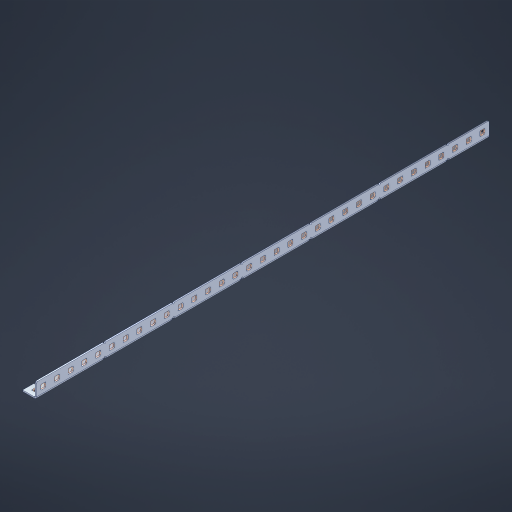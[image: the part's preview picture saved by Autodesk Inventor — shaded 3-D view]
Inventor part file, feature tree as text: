
AUTODESK INVENTOR PART (.ipt)
format: ipt  version: 2023 (Build 270158000, 158)  size: 1,292,800 bytes
history: native  units: in
note: dims shown in document units (in); Inventor stores cm internally (conversion verified against a paired STEP export)
features: other x106, extrude x97, sheet_metal_op x11, sketch x10, pattern_linear x2, mirror x1, chamfer x1
ambient origin geometry x8: Origin, YZ Plane, XZ Plane, XY Plane, X Axis, Y Axis, Z Axis, Center Point
bodies: Solid1 (feature_tree), Body (feature_tree)
feature tree (228):
  sheet_metal_op  "Flanges"
  other  "Flange Pattern Plane"
  other  "Flange Pattern Sketch"
  sheet_metal_op  "Flange Pattern"
  sheet_metal_op  "Body Pattern"
  pattern_linear  "Center Pattern"  Spacing1=0.0469in  [1 undecoded]
  other  "Arc Length"
  mirror  "Notch Mirror"
  pattern_linear  "Notch Pattern"  Spacing1=0.182in  [1 undecoded]
  chamfer  "End Chamfer"
  extrude  "Half Cut"  Depth=0.02in
  sketch  "Sketch1"  dims[d0=1.0in]
  other  "Plate1"
  sketch  "Sketch2"  dims[d1=16.5in]
  other  "Plate2"
  sheet_metal_op  "Bend1"
  sheet_metal_op  "Corner1"
  sketch  "Sketch3"  dims[d2=0.0469in]
  sketch  "Sketch7"  dims[d3=0.0469in]
  other  "Srf1"
  other  "Srf2"
  sketch  "Sketch8"  dims[d4=0.0234in]
  sketch  "Sketch9"  dims[d5=0.0938in]
  other  "Srf91"
  sheet_metal_op  "Body Pattern Sketch"
  other  "Srf92"
  sketch  "Sketch13"  dims[d6=0.0469in]
  sketch  "Sketch14"  dims[d7=0.5in d8=90.0deg d9=0.0312in]
  sketch  "Sketch15"  dims[d10=0.1875in]
  sketch  "Sketch16"  dims[d11=0.0469in d12=0.0469in d16=0.182in d17=0.02in d18=0.0469in d19=0.0in d20=0.25in d21=0.25in d38=12.9921in d40=0.5in d41=0.3937in d43=1.0in d46=0.172in d47=1.0in d48=0.0in d49=0.182in d50=0.02in d51=0.25in d52=0.25in d53=0.0469in d54=0.0in d55=0.172in d56=1.0in d57=0.0in d58=0.25in d60=12.9921in d62=0.5in d63=0.3937in d65=0.5in d85=0.1227in d86=0.1659in d88=0.04in d89=0.0469in d90=0.0in d91=0.04in d92=0.0491in d95=2.5in d96=0.04in d97=0.25in d98=45.0deg d99=0.25in d100=0.5in d101=0.0in d102=2.497in d106=0.182in d107=0.02in d108=0.5in d109=0.5in d110=0.0469in d111=0.0in d112=0.172in d113=0.5in d114=0.0in d117=0.5in d118=0.5in d119=0.5in]
  other  "Srf786"
  other  "Srf823"
  other  "Srf824"
  other  "Srf825"
  other  "Srf826"
  other  "Srf827"
  other  "Srf828"
  other  "Srf829"
  other  "Srf856"
  other  "Srf857"
  other  "Srf858"
  other  "Srf859"
  other  "Srf860"
  other  "Srf861"
  other  "Srf862"
  other  "Srf889"
  other  "Srf890"
  other  "Srf891"
  other  "Srf892"
  other  "Srf893"
  other  "Srf894"
  other  "Srf895"
  other  "Srf896"
  other  "Srf922"
  other  "Srf923"
  other  "Srf924"
  other  "Srf925"
  other  "Srf926"
  other  "Srf959"
  other  "Srf960"
  other  "Srf961"
  other  "Srf962"
  other  "Srf963"
  other  "Srf996"
  other  "Srf997"
  other  "Srf998"
  other  "Srf999"
  other  "Srf1000"
  other  "Srf1143"
  other  "Srf1144"
  other  "Srf1145"
  other  "Srf1146"
  other  "Srf1147"
  other  "Srf1148"
  other  "Srf1149"
  other  "Srf1150"
  other  "Srf1151"
  other  "Srf1152"
  other  "Srf1153"
  other  "Srf1154"
  other  "Srf1155"
  other  "Srf1156"
  other  "Srf1157"
  other  "Srf1158"
  other  "Srf1159"
  other  "Srf1160"
  other  "Srf1161"
  other  "Srf1199"
  other  "Srf1200"
  other  "Srf1201"
  other  "Srf1202"
  other  "Srf1203"
  other  "Srf1204"
  other  "Srf1205"
  other  "Srf1206"
  other  "Srf1207"
  other  "Srf1208"
  other  "Srf1209"
  other  "Srf1210"
  other  "Srf1211"
  other  "Srf1212"
  other  "Srf1213"
  other  "Srf1214"
  other  "Srf1215"
  other  "Srf1216"
  other  "Srf1217"
  other  "Srf1255"
  other  "Srf1256"
  other  "Srf1257"
  other  "Srf1258"
  other  "Srf1259"
  other  "Srf1260"
  other  "Srf1261"
  other  "Srf1262"
  other  "Srf1263"
  other  "Srf1264"
  other  "Srf1265"
  other  "Srf1266"
  other  "Srf1267"
  other  "Srf1268"
  other  "Srf1269"
  other  "Srf1270"
  other  "Srf1271"
  other  "Srf1272"
  other  "Srf1273"
  sheet_metal_op  "Flange Stamp"
  sheet_metal_op  "Flange Circle"
  sheet_metal_op  "Body Stamp"
  sheet_metal_op  "Body Circle"
  other  "Center Stamp"
  other  "Center Circle"
  sheet_metal_op  "Notch"
  extrude  "ExtrusionSrf2"  Depth=0.0469in
  extrude  "ExtrusionSrf92"  TaperAngle=0.0deg  [1 undecoded]
  extrude  "ExtrusionSrf823"  Depth=0.5in
  extrude  "ExtrusionSrf824"  Depth=0.5in
  extrude  "ExtrusionSrf825"  Depth=0.5in
  extrude  "ExtrusionSrf826"  Depth=0.5in
  extrude  "ExtrusionSrf827"  Depth=1.0in TaperAngle=0.0deg
  extrude  "ExtrusionSrf828"  Depth=0.182in
  extrude  "ExtrusionSrf829"  Depth=0.02in
  extrude  "ExtrusionSrf856"  Depth=0.5in
  extrude  "ExtrusionSrf857"  Depth=0.5in
  extrude  "ExtrusionSrf858"  Depth=0.0469in
  extrude  "ExtrusionSrf859"  TaperAngle=0.0deg  [1 undecoded]
  extrude  "ExtrusionSrf860"  Depth=0.5in
  extrude  "ExtrusionSrf861"  Depth=1.0in TaperAngle=0.0deg
  extrude  "ExtrusionSrf862"  Depth=0.5in
  extrude  "ExtrusionSrf889"  Depth=0.5in
  extrude  "ExtrusionSrf890"  Depth=0.5in
  extrude  "ExtrusionSrf891"  Depth=0.5in
  extrude  "ExtrusionSrf892"  Depth=0.5in
  extrude  "ExtrusionSrf893"  Depth=0.5in
  extrude  "ExtrusionSrf894"  Depth=0.0469in
  extrude  "ExtrusionSrf895"  TaperAngle=0.0deg  [1 undecoded]
  extrude  "ExtrusionSrf896"  Depth=0.5in
  extrude  "ExtrusionSrf922"  Depth=0.5in
  extrude  "ExtrusionSrf923"  Depth=0.5in
  extrude  "ExtrusionSrf924"  Depth=0.5in TaperAngle=45.0deg
  extrude  "ExtrusionSrf925"  Depth=0.5in
  extrude  "ExtrusionSrf926"  Depth=0.5in TaperAngle=0.0deg
  extrude  "ExtrusionSrf959"  Depth=0.5in
  extrude  "ExtrusionSrf960"  Depth=0.182in
  extrude  "ExtrusionSrf961"  Depth=0.02in
  extrude  "ExtrusionSrf962"  Depth=0.5in
  extrude  "ExtrusionSrf963"  Depth=0.5in
  extrude  "ExtrusionSrf996"  Depth=0.0469in
  extrude  "ExtrusionSrf997"  TaperAngle=0.0deg  [1 undecoded]
  extrude  "ExtrusionSrf998"  Depth=0.5in
  extrude  "ExtrusionSrf999"  Depth=0.5in TaperAngle=0.0deg
  extrude  "ExtrusionSrf1000"  Depth=0.5in
  extrude  "ExtrusionSrf1143"  Depth=0.5in
  extrude  "ExtrusionSrf1144"  Depth=0.5in
  extrude  "ExtrusionSrf1145"  [1 undecoded]
  extrude  "ExtrusionSrf1146"  [1 undecoded]
  extrude  "ExtrusionSrf1147"  [1 undecoded]
  extrude  "ExtrusionSrf1148"  [1 undecoded]
  extrude  "ExtrusionSrf1149"  [1 undecoded]
  extrude  "ExtrusionSrf1150"  [1 undecoded]
  extrude  "ExtrusionSrf1151"  [1 undecoded]
  extrude  "ExtrusionSrf1152"  [1 undecoded]
  extrude  "ExtrusionSrf1153"  [1 undecoded]
  extrude  "ExtrusionSrf1154"  [1 undecoded]
  extrude  "ExtrusionSrf1155"  [1 undecoded]
  extrude  "ExtrusionSrf1156"  [1 undecoded]
  extrude  "ExtrusionSrf1157"  [1 undecoded]
  extrude  "ExtrusionSrf1158"  [1 undecoded]
  extrude  "ExtrusionSrf1159"  [1 undecoded]
  extrude  "ExtrusionSrf1160"  [1 undecoded]
  extrude  "ExtrusionSrf1161"  [1 undecoded]
  extrude  "ExtrusionSrf1199"  [1 undecoded]
  extrude  "ExtrusionSrf1200"  [1 undecoded]
  extrude  "ExtrusionSrf1201"  [1 undecoded]
  extrude  "ExtrusionSrf1202"  [1 undecoded]
  extrude  "ExtrusionSrf1203"  [1 undecoded]
  extrude  "ExtrusionSrf1204"  [1 undecoded]
  extrude  "ExtrusionSrf1205"  [1 undecoded]
  extrude  "ExtrusionSrf1206"  [1 undecoded]
  extrude  "ExtrusionSrf1207"  [1 undecoded]
  extrude  "ExtrusionSrf1208"  [1 undecoded]
  extrude  "ExtrusionSrf1209"  [1 undecoded]
  extrude  "ExtrusionSrf1210"  [1 undecoded]
  extrude  "ExtrusionSrf1211"  [1 undecoded]
  extrude  "ExtrusionSrf1212"  [1 undecoded]
  extrude  "ExtrusionSrf1213"  [1 undecoded]
  extrude  "ExtrusionSrf1214"  [1 undecoded]
  extrude  "ExtrusionSrf1215"  [1 undecoded]
  extrude  "ExtrusionSrf1216"  [1 undecoded]
  extrude  "ExtrusionSrf1217"  [1 undecoded]
  extrude  "ExtrusionSrf1255"  [1 undecoded]
  extrude  "ExtrusionSrf1256"  [1 undecoded]
  extrude  "ExtrusionSrf1257"  [1 undecoded]
  extrude  "ExtrusionSrf1258"  [1 undecoded]
  extrude  "ExtrusionSrf1259"  [1 undecoded]
  extrude  "ExtrusionSrf1260"  [1 undecoded]
  extrude  "ExtrusionSrf1261"  [1 undecoded]
  extrude  "ExtrusionSrf1262"  [1 undecoded]
  extrude  "ExtrusionSrf1263"  [1 undecoded]
  extrude  "ExtrusionSrf1264"  [1 undecoded]
  extrude  "ExtrusionSrf1265"  [1 undecoded]
  extrude  "ExtrusionSrf1266"  [1 undecoded]
  extrude  "ExtrusionSrf1267"  [1 undecoded]
  extrude  "ExtrusionSrf1268"  [1 undecoded]
  extrude  "ExtrusionSrf1269"  [1 undecoded]
  extrude  "ExtrusionSrf1270"  [1 undecoded]
  extrude  "ExtrusionSrf1271"  [1 undecoded]
  extrude  "ExtrusionSrf1272"  [1 undecoded]
  extrude  "ExtrusionSrf1273"  [1 undecoded]
note: 61 required parameter values undecoded (feature->parameter linkage not recoverable at this tier; creation-order binding heuristic only, values carry confidence <= 0.55)
